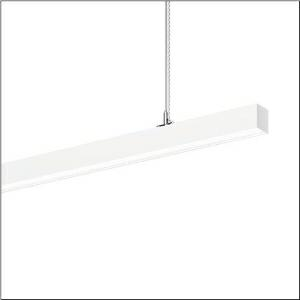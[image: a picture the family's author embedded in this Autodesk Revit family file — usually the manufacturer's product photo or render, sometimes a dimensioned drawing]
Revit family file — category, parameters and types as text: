
# Revit family: silica_r__21_51mx33db39wb_e509
name_source: partatom
category: Lighting Fixtures
units: mm (PartAtom-declared; Revit-internal decimal feet)

## family parameters
Cut with Voids When Loaded = No
Host = Face
Light Source = No
Part Type = Normal
Room Calculation Point = No
Round Connector Dimension = Use Diameter
Shared = No

## types (1)
- --- (1 x LED, 7390 lm, 51.6 W, 3000K)
    Apparent Load = 52 VA
    CIE Flux Codes = 78 96 99 55 100
    Color Rendering = 80
    Color Temperature = 3000K
    Default Elevation = 1800 mm
    Description = Silica® 21, office luminaire, primary optical cover: prismatic diffuser, of PMMA, CAT 2 (L<= 3000cd/m²), light emission: direct/indirect distribution, primary light characteristic: symmetric, installation type: suspended mounting, LED, rated luminous flux: 7.390lm, luminous efficacy: 143lm/W, light colour: 830, colour temperature: 3000K, control gear: DALI 2, with terminal, 3+2-pole, max. 2.5mm², mains connection: 220..240V, AC, 50/60Hz, rated input power: 51.6W, luminaire housing, of aluminium, traffic white (RAL 9016), length: 1.504mm, width: 53mm, height: 53mm, protection rating (complete): IP20, insulation class (complete): insulation class I (protective earthing), certification: CE, permissible operating ambient temperature: 0..+35°C, standard: EN 50419, packaging unit: 1 piece
    Height = 53 mm
    Lamp = 1 x LED
    Lamp Light Flux = 7390 lm
    Lamp Power = 51.6 W
    Lamp count = 1
    Length = 1504 mm
    Luminous efficacy = 143 lm/W
    Manufacturer = Siteco
    ModVariant = No
    Model = 51MX33DB39WB
    Mounting Place = Ceiling
    Mounting Type = Pendant
    Number of Poles = 1
    OnlyDefault = Yes
    Power Factor = 1
    Product Name = Silica® 21
    Product group = office luminaire | ceiling pendant
    ProductGroupID = 903
    Protection Class = Protection class I
    Protection Degree = IP 20
    RLX_Detail_Level = 1
    RLX_Emergency_Light_Flux = 0 lm
    RLX_Emergency_Type = 0
    RLX_Emergency_Type_DB = No
    RlxData = <blob elided: 21513 chars, md5=0c9c6820>
    Socket = socket
    Standby Power = 0 W
    System Light Flux = 7390 lm
    System Power = 52 W
    Type Comments = factory setting: luminous flux: 100 % | dim-lin: 254 | 345 mA
    Type Image = l_1349007.jpg
    URL = http://relux.com
    VarID = @adj_139773
    Voltage = 0 V
    Weight = 0.00 kg
    Width = 53 mm

## geometry (parser evidence)
native form markers: Blend x4, Sweep x11
no freeform markers — native parametric forms only
